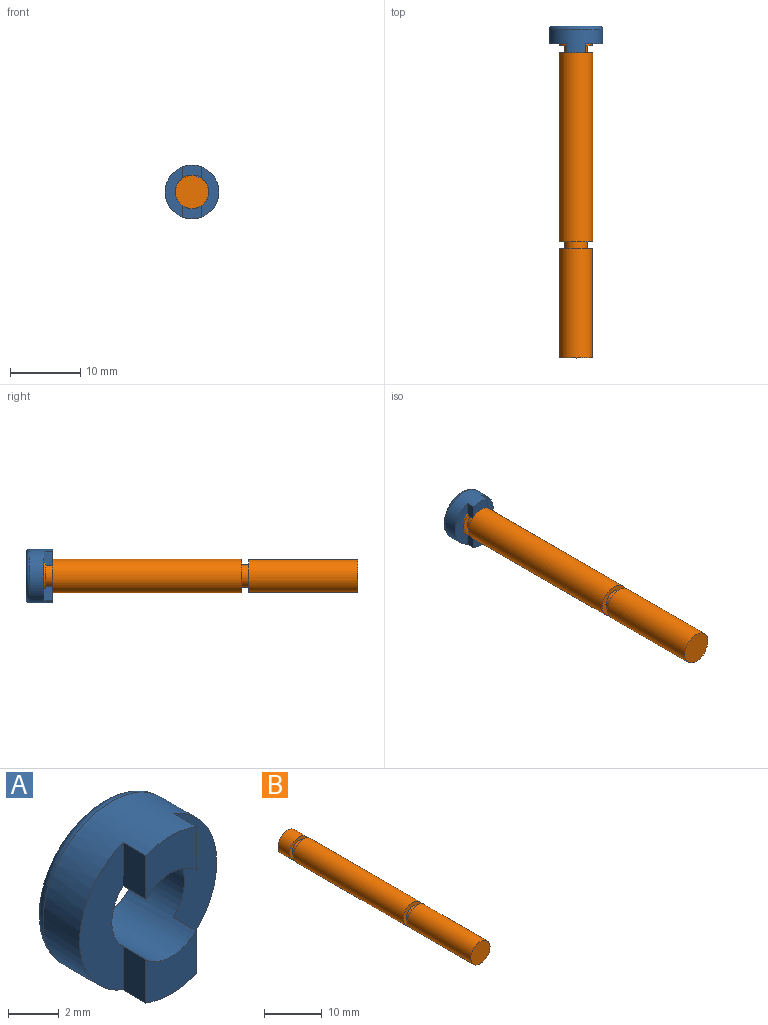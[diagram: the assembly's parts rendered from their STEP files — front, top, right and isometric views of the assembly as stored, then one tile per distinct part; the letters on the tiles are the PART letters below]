
ASSEMBLY  parts=2 mates=1
PART A: 12 faces, bbox 8.2x3.8x8.2 mm
  f0: cylinder r=3.81mm len=7.62mm, axis (0,-1,0), area 55.9mm2, adj f1,f2,f5,f6,f7,f8,f9,f10
  f1: plane 2.79x2.35mm, normal (0,-1,0), area 5.2mm2, adj f0,f3,f6,f10
  f2: plane 2.79x2.35mm, normal (0,-1,0), area 5.2mm2, adj f0,f3,f5,f8
  f3: cylinder r=2.02mm len=4.04mm, axis (0,-1,0), area 40.1mm2, adj f1,f2,f4,f5,f6,f7,f8,f9
  f4: plane 6.6x6.6mm, normal (0,1,0), area 21.4mm2, adj f3,f11
  f5: plane 2.09x1.27mm, normal (-1,0,0), area 2.6mm2, adj f0,f2,f3,f7
  f6: plane 2.09x1.27mm, normal (-1,0,0), area 2.6mm2, adj f0,f1,f3,f7
  f7: plane 7.09x2.41mm, normal (0,-1,0), area 11.1mm2, adj f0,f3,f5,f6
  f8: plane 2.09x1.27mm, normal (1,0,0), area 2.6mm2, adj f0,f2,f3,f9
  f9: plane 7.09x2.41mm, normal (0,-1,0), area 11.1mm2, adj f0,f3,f8,f10
  f10: plane 2.09x1.27mm, normal (1,0,0), area 2.6mm2, adj f0,f1,f3,f9
  f11: torus R=3.3mm, axis (0,-1,0), area 18.2mm2, adj f0,f4
PART B: 11 faces, bbox 4.8x47.1x4.8 mm
  f0: plane 4.67x4.67mm, normal (0,-1,0), area 8.9mm2, adj f1,f10
  f1: cylinder r=1.62mm len=3.24mm, axis (0,-1,0), area 10.3mm2, adj f0,f2
  f2: plane 4.76x4.76mm, normal (0,1,0), area 9.6mm2, adj f1,f3
  f3: cylinder r=2.38mm len=26.8mm, axis (0,-1,0), area 400.9mm2, adj f2,f4
  f4: plane 4.76x4.76mm, normal (0,-1,0), area 9.6mm2, adj f3,f5
  f5: cylinder r=1.62mm len=3.24mm, axis (0,-1,0), area 10.3mm2, adj f4,f6
  f6: plane 4.67x4.67mm, normal (0,1,0), area 8.9mm2, adj f5,f7
  f7: cylinder r=2.34mm len=15.49mm, axis (0,-1,0), area 227.5mm2, adj f6,f8
  f8: plane 4.67x4.67mm, normal (0,-1,0), area 17.2mm2, adj f7
  f9: plane 4.67x4.67mm, normal (0,1,0), area 17.2mm2, adj f10
  f10: cylinder r=2.34mm len=4.67mm, axis (0,-1,0), area 41mm2, adj f0,f9
PLACE A t=(0,8.38,0)mm
PLACE B at identity fixed
MATE fastened A.f3 <-> B.f1  axis (0,-1,0) through (0,8.38,0)mm
